# Revit family: Считыватель AGRG AXI 1_тип модель
name_source: partatom
category: Охранная сигнализация
units: mm (PartAtom-declared; Revit-internal decimal feet)

## family parameters
Всегда вертикально = Да
На основе рабочей плоскости = Нет
Общий = Нет
При загрузке вырезать с полостями = Нет
Размер круглого соединителя = Использовать диаметр
Сохранять ориентацию аннотаций = Нет
Тип детали = Нормальный
Точка расчета площади = Нет

## types (3) — shared parameters
ADSK_Верхний порог напряжения = 15 В
ADSK_Группирование = 1. Оборудование
ADSK_Единица измерения = шт.
ADSK_Завод-изготовитель = ООО «Агрегатор»
ADSK_Количество = 1
ADSK_Марка = AGRG AXI
ADSK_Масса = 0.06
ADSK_Наименование краткое = Считыватель бесконтактных карт
ADSK_Нижний порог напряжения = 9 В
ADSK_Обозначение = RC
ITV_SUB_УГО на структурной схеме = УГО_Считыватель
URL = https://skud.agrg.ru
Изображение типоразмера = RC.png
Описание = ITV
Стоимость = 14250 $

## per-type parameters (varying)
| type | ADSK_Код изделия | ADSK_Наименование | Материал |
| Считыватель AGRG AXI 1 «Арктический белый» | AXI1AW | Считыватель для СКУД AGRG AXI 1 "Арктический белый"; Интерфейс: W-26, 34, 58; Чтение идентификаторов соответствующих стандарту ISO/IEC 14443A MIFARE (UID) Mifare Mini, Mifare Classic, Mifare Plus SL1/SL3, Mifare DESFire (только UID ); TM (DS1990A) - поддержка всех вышеуказанных форматов; Размер, мм: 82x38x10; Материал корпуса: искусственный камень на базе акрила | Пластмасса, непрозрачная, белая |
| Считыватель AGRG AXI 1 «Люксовый Мандарин» | AXI1LM | Считыватель для СКУД AGRG AXI 1 "Люксовый мандарин"; Интерфейс: W-26, 34, 58; Чтение идентификаторов соответствующих стандарту ISO/IEC 14443A MIFARE (UID) Mifare Mini, Mifare Classic, Mifare Plus SL1/SL3, Mifare DESFire (только UID ); TM (DS1990A) - поддержка всех вышеуказанных форматов; Размер, мм: 82x38x10; Материал корпуса: искусственный камень на базе акрила | Пластмасса, непрозрачная, оранжевая |
| Считыватель AGRG AXI 1 «Имперский черный» | AXI1IBL | Считыватель для СКУД AGRG AXI 1 "Имперский черный"; Интерфейс: W-26, 34, 58; Чтение идентификаторов соответствующих стандарту ISO/IEC 14443A MIFARE (UID) Mifare Mini, Mifare Classic, Mifare Plus SL1/SL3, Mifare DESFire (только UID ); TM (DS1990A) - поддержка всех вышеуказанных форматов; Размер, мм: 82x38x10; Материал корпуса: искусственный камень на базе акрила | Пластмасса, непрозрачная, черная |
